# Revit family: 603-A-6100-DN300
name_source: partatom
category: Pipe Accessories
units: mm (PartAtom-declared; Revit-internal decimal feet)

## family parameters
Always vertical = Yes
Cut with Voids When Loaded = No
Part Type = Valve - Breaks Into
Round Connector Dimension = Use Diameter
Shared = No
Work Plane-Based = No

## types (2) — shared parameters
Bolt_width = 20 mm  [stored 0.0656168 ft]
Bottm_cut = 184 mm
Bottm_height = 8 mm  [stored 0.0262467 ft]
Bottom_Flange_Thicckness = 12 mm  [stored 0.0393701 ft]
D = 242 mm  [stored 0.793963 ft]
D2 = 185 mm  [stored 0.606955 ft]
D3 = 200 mm  [stored 0.656168 ft]
D4 = 222 mm
DN300_301 - 327 = 603-327-000-6100
DN300_324 - 350 = 603-350-000-6100
Description_ = AVK UNIVERSAL SUPA® FLANGE ADAPTOR
H1 = 33 mm  [stored 0.108268 ft]
ID = 150 mm  [stored 0.492126 ft]
L = 99 mm  [stored 0.324803 ft]
L1 = 61 mm  [stored 0.200131 ft]
Max_Height = 170 mm  [stored 0.557743 ft]
Nomianal_Diameter(DN) = 300 mm  [stored 0.984252 ft]
Nut = 10 mm  [stored 0.0328084 ft]
PCD = 420 mm  [stored 1.37795 ft]
Rib_Thickness = 5 mm  [stored 0.0164042 ft]
Rib_length = 32 mm  [stored 0.104987 ft]
Rib_width = 445 mm  [stored 1.45997 ft]
Search_table = 603-A-6100-DN300
URL product pages = https://www.avkvalves.com
Washer = 3 mm  [stored 0.00984252 ft]

## per-type parameters (varying)
| type | Bolt_Ref | DN1 | DN1_ref | DN2 | DN2_ref | Washer_Ref |
| DN300_301 - 327 | 26 mm | 164 mm | 327 mm | 151 mm  [stored 0.495407 ft] | 301 mm  [stored 0.987533 ft] | 36 mm |
| DN300_324 - 350 | 14 mm  [stored 0.0459318 ft] | 175 mm  [stored 0.574147 ft] | 350 mm  [stored 1.14829 ft] | 162 mm  [stored 0.531496 ft] | 324 mm  [stored 1.06299 ft] | 24 mm  [stored 0.0787402 ft] |

note: [stored X ft] marks values corroborated as IEEE doubles in the binary element streams (Revit-internal decimal feet)

## geometry (parser evidence)
native form markers: Sweep x9
no freeform markers — native parametric forms only
